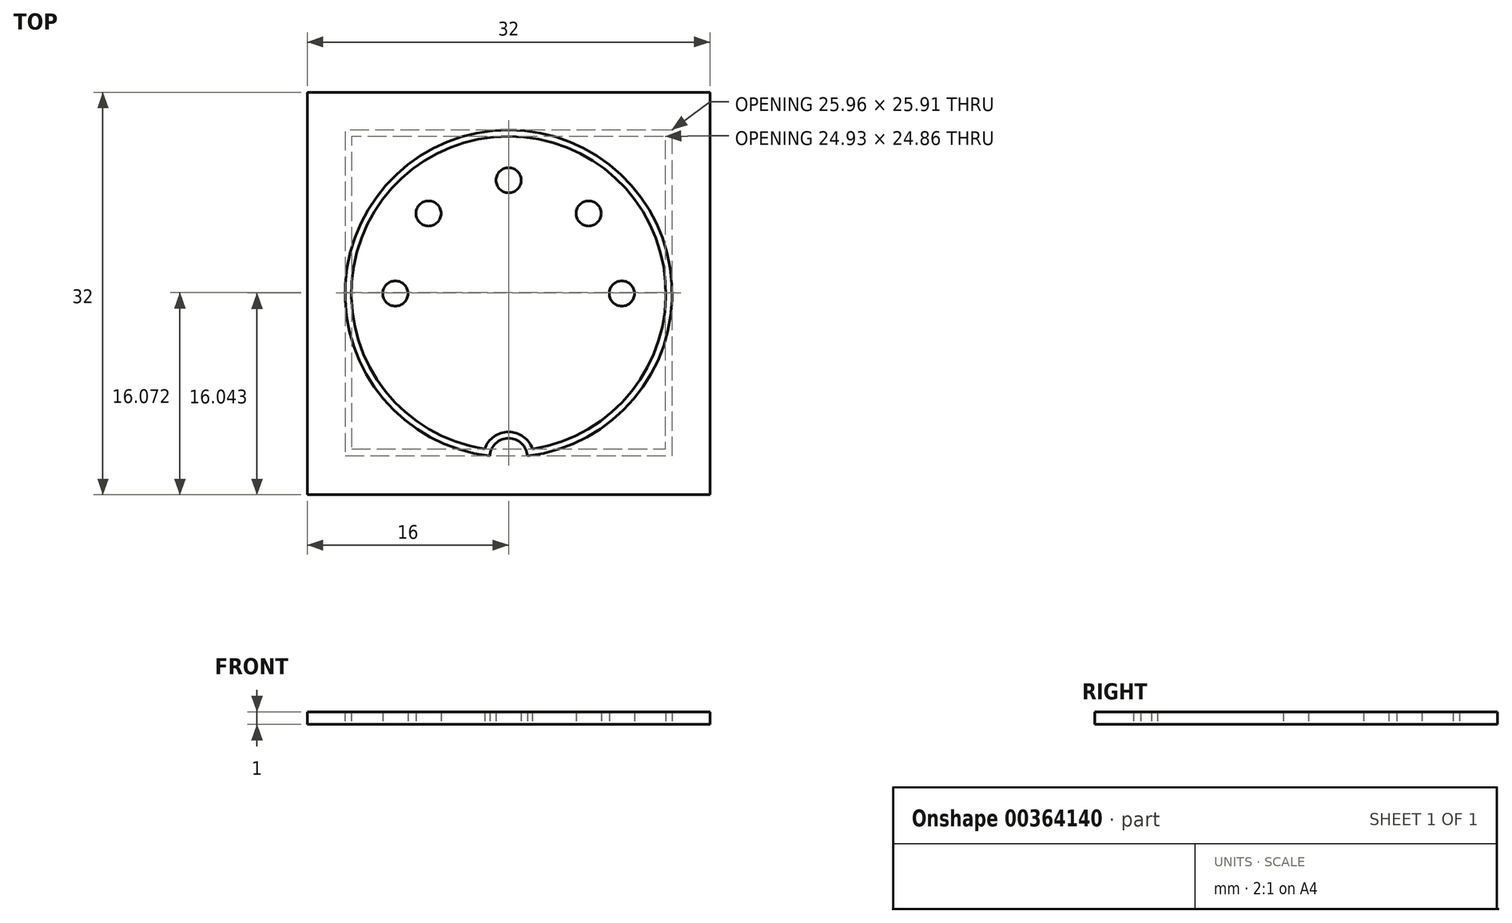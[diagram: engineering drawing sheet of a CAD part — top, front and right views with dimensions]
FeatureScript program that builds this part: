
annotation { "Feature Type Name" : "Feature", "Feature Type Description" : "" }
export const myFeature = defineFeature(function(context is Context, id is Id, definition is map)
    precondition{}
    {
        {
            var Q0;
            Q0=qCreatedBy(makeId("Top.planeOp"),FACE);
            var sketch = newSketch(context, id + "F0", { "sketchPlane" : qUnion([Q0])});
            skArc(sketch, "E0", {"start": v(1.9, -12.36) * mm, "mid": v(0, 12.5) * mm, "end": v(-1.9, -12.36) * mm});
            skCircle(sketch, "E1", {"center": v(0, 9) * mm, "radius": 1 * mm});
            skCircle(sketch, "E2", {"center": v(-9, 0) * mm, "radius": 1 * mm});
            skCircle(sketch, "E3", {"center": v(9, 0) * mm, "radius": 1 * mm});
            skCircle(sketch, "E4", {"center": v(-6.36, 6.36) * mm, "radius": 1 * mm});
            skCircle(sketch, "E5", {"center": v(6.36, 6.36) * mm, "radius": 1 * mm});
            skArc(sketch, "E6", {"start": v(1.5, -12.91) * mm, "mid": v(0, 13) * mm, "end": v(-1.5, -12.91) * mm});
            skArc(sketch, "E7", {"start": v(1.5, -12.91) * mm, "mid": v(0, -11.5) * mm, "end": v(-1.5, -12.91) * mm});
            skArc(sketch, "E8", {"start": v(1.9, -12.36) * mm, "mid": v(0, -11) * mm, "end": v(-1.9, -12.36) * mm});
            skLineSegment(sketch, "E9.bottom", {"start": v(16, 16) * mm, "end": v(-16, 16) * mm});
            skLineSegment(sketch, "E9.top", {"start": v(16, -16) * mm, "end": v(-16, -16) * mm});
            skLineSegment(sketch, "E9.left", {"start": v(16, 16) * mm, "end": v(16, -16) * mm});
            skLineSegment(sketch, "E9.right", {"start": v(-16, 16) * mm, "end": v(-16, -16) * mm});
            skSolve(sketch);
        }
        {
            var Q0;
            Q0=makeQuery(id+"F0.imprint","IMPRINT",FACE,{"disambiguationData":[TD([[makeQuery(id+"F0.imprint","IMPRINT",EDGE,{"derivedFrom":sQuery(id+"F0.wireOp",EDGE,"E4")}),1.0]])]});
            var Q1;
            Q1=makeQuery(id+"F0.imprint","IMPRINT",FACE,{"disambiguationData":[TD([[makeQuery(id+"F0.imprint","IMPRINT",EDGE,{"derivedFrom":sQuery(id+"F0.wireOp",EDGE,"E2")}),1.0]])]});
            var Q2;
            Q2=makeQuery(id+"F0.imprint","IMPRINT",FACE,{"disambiguationData":[TD([[makeQuery(id+"F0.imprint","IMPRINT",EDGE,{"derivedFrom":sQuery(id+"F0.wireOp",EDGE,"E1")}),1.0]])]});
            var Q3;
            Q3=makeQuery(id+"F0.imprint","IMPRINT",FACE,{"disambiguationData":[TD([[makeQuery(id+"F0.imprint","IMPRINT",EDGE,{"derivedFrom":sQuery(id+"F0.wireOp",EDGE,"E5")}),1.0]])]});
            var Q4;
            Q4=makeQuery(id+"F0.imprint","IMPRINT",FACE,{"disambiguationData":[TD([[makeQuery(id+"F0.imprint","IMPRINT",EDGE,{"derivedFrom":sQuery(id+"F0.wireOp",EDGE,"E3")}),1.0]])]});
            var Q5;
            Q5=makeQuery(id+"F0.imprint","IMPRINT",FACE,{"disambiguationData":[TD([[makeQuery(id+"F0.imprint","IMPRINT",EDGE,{"derivedFrom":sQuery(id+"F0.wireOp",EDGE,"E0")}),-1.0]])]});
            extrude(context, id + "F1", {"entities" : qUnion([Q0, Q1, Q2, Q3, Q4, Q5]), "depth" : 1 * mm});
        }
        {
            var Q0;
            Q0=makeQuery(id+"F0.imprint","IMPRINT",FACE,{"disambiguationData":[TD([[makeQuery(id+"F0.imprint","IMPRINT",EDGE,{"derivedFrom":sQuery(id+"F0.wireOp",EDGE,"E6")}),-1.0]])]});
            extrude(context, id + "F2", {"entities" : qUnion([Q0]), "depth" : 1 * mm});
        }
    });
